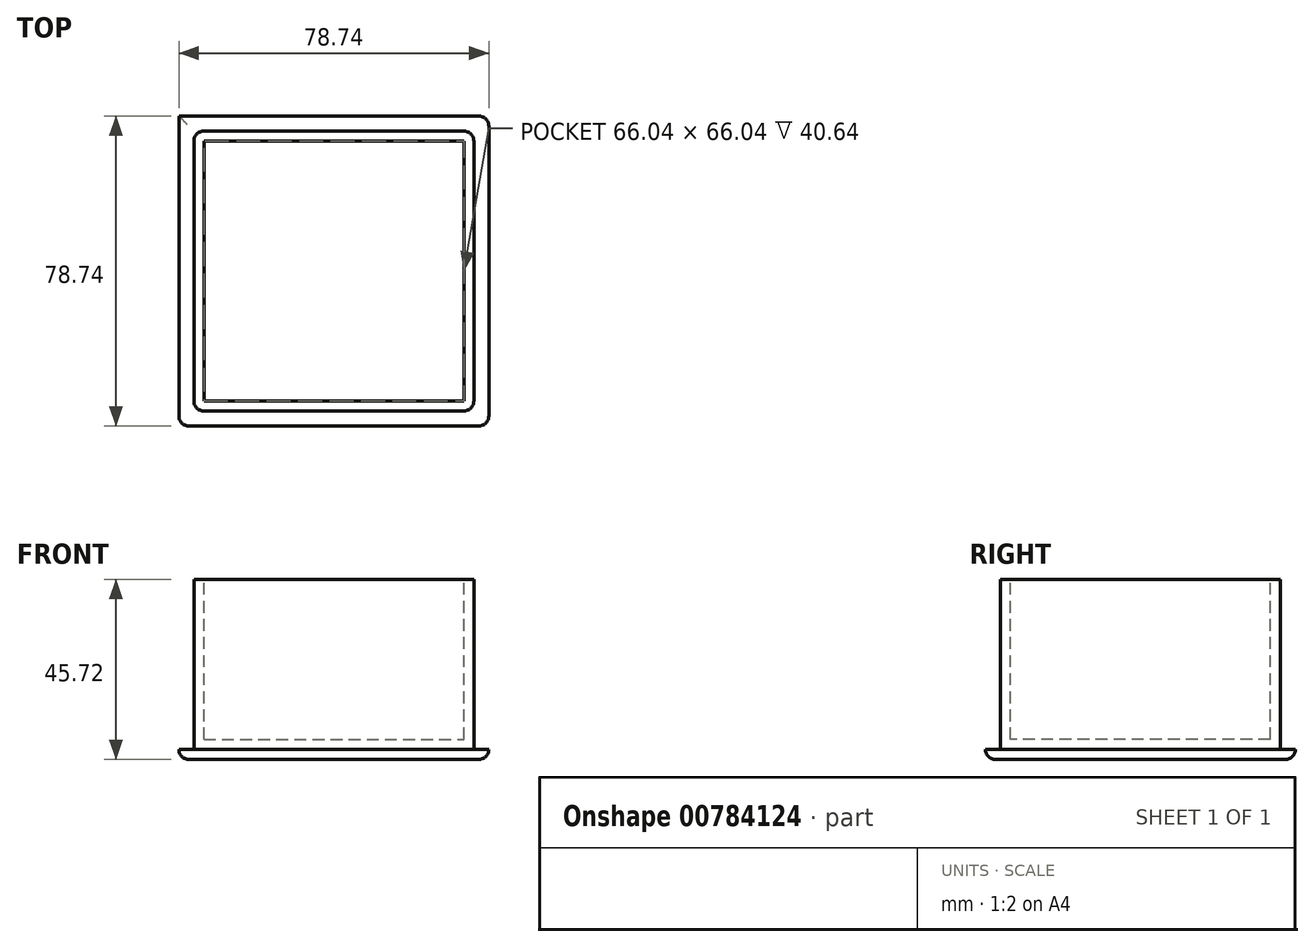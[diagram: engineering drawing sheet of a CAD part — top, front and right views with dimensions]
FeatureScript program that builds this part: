
annotation { "Feature Type Name" : "Feature", "Feature Type Description" : "" }
export const myFeature = defineFeature(function(context is Context, id is Id, definition is map)
    precondition{}
    {
        {
            var Q0;
            Q0=qCreatedBy(makeId("Top.planeOp"),FACE);
            var sketch = newSketch(context, id + "F0", { "sketchPlane" : qUnion([Q0])});
            skLineSegment(sketch, "E0.bottom", {"start": v(0, 0) * mm, "end": v(71.12, 0) * mm});
            skLineSegment(sketch, "E0.top", {"start": v(0, 71.12) * mm, "end": v(71.12, 71.12) * mm});
            skLineSegment(sketch, "E0.left", {"start": v(0, 0) * mm, "end": v(0, 71.12) * mm});
            skLineSegment(sketch, "E0.right", {"start": v(71.12, 0) * mm, "end": v(71.12, 71.12) * mm});
            skSolve(sketch);
        }
        {
            var Q0;
            Q0=makeQuery(id+"F0.imprint","IMPRINT",FACE,{"disambiguationData":[TD([[makeQuery(id+"F0.imprint","IMPRINT",EDGE,{"derivedFrom":sQuery(id+"F0.wireOp",EDGE,"E0.bottom")}),1.0]])]});
            extrude(context, id + "F1", {"entities" : qUnion([Q0]), "depth" : 43.18 * mm, "offsetDistance" : 25.4 * mm});
        }
        {
            var Q0;
            Q0=makeQuery(id+"F1.opExtrude","CAP_FACE",FACE,{"disambiguationData":[OSD([sQuery(id+"F0.wireOp",EDGE,"E0.bottom"),sQuery(id+"F0.wireOp",EDGE,"E0.top"),sQuery(id+"F0.wireOp",EDGE,"E0.left"),sQuery(id+"F0.wireOp",EDGE,"E0.right")])],"isStart":false});
            var sketch = newSketch(context, id + "F2", { "sketchPlane" : qUnion([Q0])});
            skLineSegment(sketch, "E1.bottom", {"start": v(0, 71.12) * mm, "end": v(2.54, 71.12) * mm});
            skLineSegment(sketch, "E1.top", {"start": v(0, 68.58) * mm, "end": v(2.54, 68.58) * mm});
            skLineSegment(sketch, "E1.left", {"start": v(0, 71.12) * mm, "end": v(0, 68.58) * mm});
            skLineSegment(sketch, "E1.right", {"start": v(2.54, 71.12) * mm, "end": v(2.54, 68.58) * mm});
            skLineSegment(sketch, "E2.bottom", {"start": v(2.54, 68.58) * mm, "end": v(68.58, 68.58) * mm});
            skLineSegment(sketch, "E2.top", {"start": v(2.54, 2.54) * mm, "end": v(68.58, 2.54) * mm});
            skLineSegment(sketch, "E2.left", {"start": v(2.54, 68.58) * mm, "end": v(2.54, 2.54) * mm});
            skLineSegment(sketch, "E2.right", {"start": v(68.58, 68.58) * mm, "end": v(68.58, 2.54) * mm});
            skSolve(sketch);
        }
        {
            var Q0;
            Q0=makeQuery(id+"F2.imprint","IMPRINT",FACE,{"disambiguationData":[TD([[makeQuery(id+"F2.imprint","IMPRINT",EDGE,{"derivedFrom":sQuery(id+"F2.wireOp",EDGE,"E2.bottom")}),-1.0]])]});
            extrude(context, id + "F3", {"entities" : qUnion([Q0]), "operationType" : NewBodyOperationType.REMOVE, "oppositeDirection" : true, "depth" : 40.64 * mm, "offsetDistance" : 25.4 * mm});
        }
        {
            var Q0;
            Q0=makeQuery(id+"F1.opExtrude","CAP_FACE",FACE,{"disambiguationData":[OSD([sQuery(id+"F0.wireOp",EDGE,"E0.bottom"),sQuery(id+"F0.wireOp",EDGE,"E0.top"),sQuery(id+"F0.wireOp",EDGE,"E0.left"),sQuery(id+"F0.wireOp",EDGE,"E0.right")])],"isStart":true});
            var sketch = newSketch(context, id + "F4", { "sketchPlane" : qUnion([Q0])});
            skPoint(sketch, "E3.firstSnap0", {"position": v(0, -35.56) * mm});
            skPoint(sketch, "E3.firstSnap1", {"position": v(35.56, -71.12) * mm});
            skLineSegment(sketch, "E4.bottom", {"start": v(0, -71.12) * mm, "end": v(-3.81, -71.12) * mm});
            skLineSegment(sketch, "E4.top", {"start": v(0, -74.93) * mm, "end": v(-3.81, -74.93) * mm});
            skLineSegment(sketch, "E4.left", {"start": v(0, -71.12) * mm, "end": v(0, -74.93) * mm});
            skLineSegment(sketch, "E4.right", {"start": v(-3.81, -71.12) * mm, "end": v(-3.81, -74.93) * mm});
            skLineSegment(sketch, "E5.bottom", {"start": v(-3.81, -74.93) * mm, "end": v(74.93, -74.93) * mm});
            skLineSegment(sketch, "E5.top", {"start": v(-3.81, 3.81) * mm, "end": v(74.93, 3.81) * mm});
            skLineSegment(sketch, "E5.left", {"start": v(-3.81, -74.93) * mm, "end": v(-3.81, 3.81) * mm});
            skLineSegment(sketch, "E5.right", {"start": v(74.93, -74.93) * mm, "end": v(74.93, 3.81) * mm});
            skSolve(sketch);
        }
        {
            var Q0;
            Q0=makeQuery(id+"F1.opExtrude","SWEPT_EDGE",EDGE,{"disambiguationData":[OSD([sQuery(id+"F0.wireOp",EDGE,"E0.bottom"),sQuery(id+"F0.wireOp",EDGE,"E0.right")])]});
            var Q1;
            Q1=makeQuery(id+"F1.opExtrude","SWEPT_EDGE",EDGE,{"disambiguationData":[OSD([sQuery(id+"F0.wireOp",EDGE,"E0.bottom"),sQuery(id+"F0.wireOp",EDGE,"E0.left")])]});
            var Q2;
            Q2=makeQuery(id+"F1.opExtrude","SWEPT_EDGE",EDGE,{"disambiguationData":[OSD([sQuery(id+"F0.wireOp",EDGE,"E0.top"),sQuery(id+"F0.wireOp",EDGE,"E0.left")])]});
            var Q3;
            Q3=makeQuery(id+"F1.opExtrude","SWEPT_EDGE",EDGE,{"disambiguationData":[OSD([sQuery(id+"F0.wireOp",EDGE,"E0.top"),sQuery(id+"F0.wireOp",EDGE,"E0.right")])]});
            fillet(context, id + "F5", {"entities" : qUnion([Q0, Q1, Q2, Q3]), "radius" : 2.54 * mm, "tangentPropagation" : true, "allowEdgeOverflow" : false});
        }
        {
            var Q0;
            {var subQ4=sQuery(id+"F4.wireOp",EDGE,"E4.bottom");Q0=makeQuery(id+"F4.imprint","IMPRINT",FACE,{"disambiguationData":[TD([[makeQuery(id+"F4.imprint","IMPRINT",EDGE,{"derivedFrom":subQ4}),-1.0]])]});}
            var Q1;
            {var subQ0=sQuery(id+"F4.wireOp",EDGE,"E4.bottom");Q1=makeQuery(id+"F4.imprint","IMPRINT",FACE,{"disambiguationData":[TD([[makeQuery(id+"F4.imprint","IMPRINT",EDGE,{"derivedFrom":subQ0}),1.0]])]});}
            var Q2;
            Q2=makeQuery(id+"F4.imprint","IMPRINT",FACE,{"disambiguationData":[TD([[makeQuery(id+"F4.imprint","IMPRINT",EDGE,{"derivedFrom":makeQuery(id+"F1.opExtrude","CAP_EDGE",EDGE,{"disambiguationData":[OSD([sQuery(id+"F0.wireOp",EDGE,"E0.bottom")])],"isStart":true})}),-1.0]])]});
            extrude(context, id + "F6", {"entities" : qUnion([Q0, Q1, Q2]), "operationType" : NewBodyOperationType.ADD, "depth" : 2.54 * mm, "offsetDistance" : 25.4 * mm});
        }
        {
            var Q0;
            Q0=makeQuery(id+"F6.opExtrude","CAP_FACE",FACE,{"disambiguationData":[OSD([sQuery(id+"F4.wireOp",EDGE,"E5.bottom"),sQuery(id+"F4.wireOp",EDGE,"E5.top"),sQuery(id+"F4.wireOp",EDGE,"E5.left"),sQuery(id+"F4.wireOp",EDGE,"E5.right")])],"isStart":false});
            var Q1;
            Q1=makeQuery(id+"F6.opExtrude","SWEPT_EDGE",EDGE,{"disambiguationData":[OSD([sQuery(id+"F4.wireOp",EDGE,"E5.bottom"),sQuery(id+"F4.wireOp",EDGE,"E5.left")])]});
            var Q2;
            Q2=makeQuery(id+"F6.opExtrude","SWEPT_EDGE",EDGE,{"disambiguationData":[OSD([sQuery(id+"F4.wireOp",EDGE,"E5.bottom"),sQuery(id+"F4.wireOp",EDGE,"E5.right")])]});
            var Q3;
            Q3=makeQuery(id+"F6.opExtrude","SWEPT_EDGE",EDGE,{"disambiguationData":[OSD([sQuery(id+"F4.wireOp",EDGE,"E5.top"),sQuery(id+"F4.wireOp",EDGE,"E5.right")])]});
            var Q4;
            Q4=makeQuery(id+"F6.opExtrude","SWEPT_EDGE",EDGE,{"disambiguationData":[OSD([sQuery(id+"F4.wireOp",EDGE,"E5.top"),sQuery(id+"F4.wireOp",EDGE,"E5.left")])]});
            fillet(context, id + "F7", {"entities" : qUnion([Q0, Q1, Q2, Q3, Q4]), "radius" : 2.54 * mm, "tangentPropagation" : true, "allowEdgeOverflow" : false});
        }
    });
